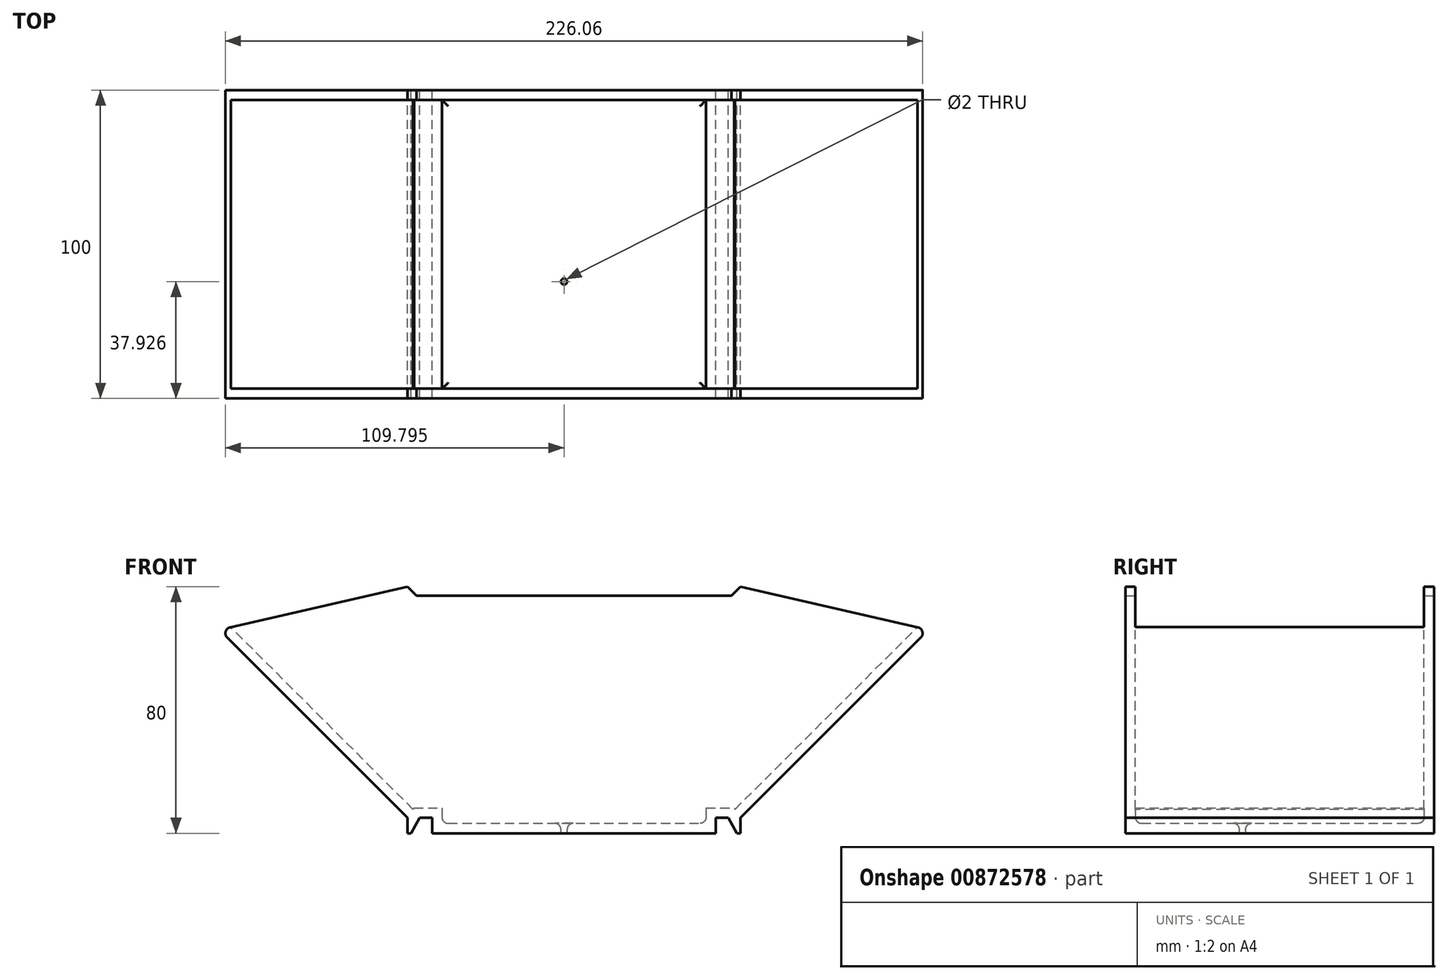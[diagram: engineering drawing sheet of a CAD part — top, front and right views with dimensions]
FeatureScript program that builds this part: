
annotation { "Feature Type Name" : "Feature", "Feature Type Description" : "" }
export const myFeature = defineFeature(function(context is Context, id is Id, definition is map)
    precondition{}
    {
        {
            var Q0;
            Q0=qCreatedBy(makeId("Front.planeOp"),FACE);
            var sketch = newSketch(context, id + "F0", { "sketchPlane" : qUnion([Q0])});
            skLineSegment(sketch, "E0.bottom", {"start": v(-50, 0) * mm, "end": v(-46, 0) * mm});
            skPoint(sketch, "E0.middle", {"position": v(0, 37.5) * mm});
            skLineSegment(sketch, "E1", {"start": v(-54, 0) * mm, "end": v(-115, 61) * mm});
            skLineSegment(sketch, "E2", {"start": v(-115, 61) * mm, "end": v(-54, 75) * mm});
            skLineSegment(sketch, "E3", {"start": v(54, 0) * mm, "end": v(115, 61) * mm});
            skLineSegment(sketch, "E4", {"start": v(115, 61) * mm, "end": v(54, 75) * mm});
            skLineSegment(sketch, "E5", {"start": v(-54, 75) * mm, "end": v(-54, 0) * mm, "construction": true});
            skLineSegment(sketch, "E6", {"start": v(54, 75) * mm, "end": v(54, 0) * mm, "construction": true});
            skLineSegment(sketch, "E7.top", {"start": v(-46, -5) * mm, "end": v(46, -5) * mm});
            skLineSegment(sketch, "E7.left", {"start": v(-46, 0) * mm, "end": v(-46, -5) * mm});
            skLineSegment(sketch, "E7.right", {"start": v(46, 0) * mm, "end": v(46, -5) * mm});
            skPoint(sketch, "E7.middle", {"position": v(0, -31.97) * mm});
            skPoint(sketch, "E7.bottom.start.orphan", {"position": v(-46, -58.94) * mm});
            skPoint(sketch, "E8.orphan", {"position": v(46, -58.94) * mm});
            skLineSegment(sketch, "E9.trimOffspring", {"start": v(46, 0) * mm, "end": v(50, 0) * mm});
            skLineSegment(sketch, "E10", {"start": v(0, 0) * mm, "end": v(0, 96.73) * mm, "construction": true});
            skLineSegment(sketch, "E11.top", {"start": v(51, 72) * mm, "end": v(-51, 72) * mm});
            skPoint(sketch, "E11.middle", {"position": v(0, 73.5) * mm});
            skLineSegment(sketch, "E12", {"start": v(-54, 0) * mm, "end": v(-54, -5) * mm});
            skLineSegment(sketch, "E13", {"start": v(54, 0) * mm, "end": v(54, -5) * mm});
            skLineSegment(sketch, "E14", {"start": v(54, -5) * mm, "end": v(52.8, -5) * mm});
            skLineSegment(sketch, "E15", {"start": v(50, 0) * mm, "end": v(52.8, -5) * mm});
            skLineSegment(sketch, "E16", {"start": v(-54, -5) * mm, "end": v(-52.8, -5) * mm});
            skLineSegment(sketch, "E17", {"start": v(-52.8, -5) * mm, "end": v(-50, 0) * mm});
            skLineSegment(sketch, "E18", {"start": v(51, 72) * mm, "end": v(54, 75) * mm});
            skLineSegment(sketch, "E19", {"start": v(-51, 72) * mm, "end": v(-54, 75) * mm});
            skSolve(sketch);
        }
        {
            var Q0;
            Q0 = qSketchRegion(id + "F0", true);
            extrude(context, id + "F1", {"entities" : qUnion([Q0]), "endBound" : BoundingType.SYMMETRIC, "depth" : 100 * mm, "offsetDistance" : 25 * mm});
        }
        {
            var Q0;
            Q0=makeQuery(id+"F1.opExtrude","SWEPT_FACE",FACE,{"disambiguationData":[OSD([sQuery(id+"F0.wireOp",EDGE,"E0.top")])]});
            var Q1;
            Q1=makeQuery(id+"F1.opExtrude","SWEPT_FACE",FACE,{"disambiguationData":[OSD([sQuery(id+"F0.wireOp",EDGE,"E2")])]});
            var Q2;
            Q2=makeQuery(id+"F1.opExtrude","SWEPT_FACE",FACE,{"disambiguationData":[OSD([sQuery(id+"F0.wireOp",EDGE,"E4")])]});
            shell(context, id + "F2", {"entities" : qUnion([Q0, Q1, Q2]), "thickness" : 3.2 * mm});
        }
        {
            var Q0;
            Q0=qCreatedBy(makeId("Top.planeOp"),FACE);
            var sketch = newSketch(context, id + "F3", { "sketchPlane" : qUnion([Q0])});
            skCircle(sketch, "E20", {"center": v(-3.24, -12.07) * mm, "radius": 1 * mm});
            skLineSegment(sketch, "E21", {"start": v(0, 0) * mm, "end": v(-9.05, -33.76) * mm, "construction": true});
            skCircle(sketch, "E22", {"center": v(0, 0) * mm, "radius": 12.5 * mm, "construction": true});
            skSolve(sketch);
        }
        {
            var Q0;
            Q0 = qSketchRegion(id + "F3", true);
            extrude(context, id + "F4", {"entities" : qUnion([Q0]), "operationType" : NewBodyOperationType.REMOVE, "endBound" : BoundingType.THROUGH_ALL, "oppositeDirection" : true, "depth" : 25 * mm, "offsetDistance" : 25 * mm});
        }
        {
            var Q0;
            Q0=qCreatedBy(makeId("Right.planeOp"),FACE);
            var sketch = newSketch(context, id + "F5", { "sketchPlane" : qUnion([Q0])});
            skLineSegment(sketch, "E23.bottom", {"start": v(46.8, 115) * mm, "end": v(-46.8, 115) * mm});
            skLineSegment(sketch, "E23.top", {"start": v(46.8, 65) * mm, "end": v(-46.8, 65) * mm});
            skLineSegment(sketch, "E23.left", {"start": v(46.8, 115) * mm, "end": v(46.8, 65) * mm});
            skLineSegment(sketch, "E23.right", {"start": v(-46.8, 115) * mm, "end": v(-46.8, 65) * mm});
            skPoint(sketch, "E23.middle", {"position": v(0, 90) * mm});
            skSolve(sketch);
        }
        {
            var Q0;
            Q0 = qSketchRegion(id + "F5", true);
            extrude(context, id + "F6", {"entities" : qUnion([Q0]), "operationType" : NewBodyOperationType.REMOVE, "endBound" : BoundingType.SYMMETRIC, "oppositeDirection" : true, "depth" : 300 * mm, "offsetDistance" : 25 * mm});
        }
        {
            var Q0;
            Q0=makeQuery(id+"F1.opExtrude","SWEPT_EDGE",EDGE,{"disambiguationData":[OSD([sQuery(id+"F0.wireOp",EDGE,"E3"),sQuery(id+"F0.wireOp",EDGE,"E4")])]});
            var Q1;
            Q1=makeQuery(id+"F1.opExtrude","SWEPT_EDGE",EDGE,{"disambiguationData":[OSD([sQuery(id+"F0.wireOp",EDGE,"E1"),sQuery(id+"F0.wireOp",EDGE,"E2")])]});
            fillet(context, id + "F7", {"entities" : qUnion([Q0, Q1]), "radius" : 2 * mm, "tangentPropagation" : true, "allowEdgeOverflow" : false});
        }
        {
            var Q0;
            Q0=makeQuery(id+"F2.opShell","OFFSET_FACE",FACE,{"disambiguationData":[OSD([sQuery(id+"F0.wireOp",EDGE,"E7.top")])]});
            fillet(context, id + "F8", {"entities" : qUnion([Q0]), "radius" : 2 * mm, "tangentPropagation" : true, "allowEdgeOverflow" : false});
        }
    });
